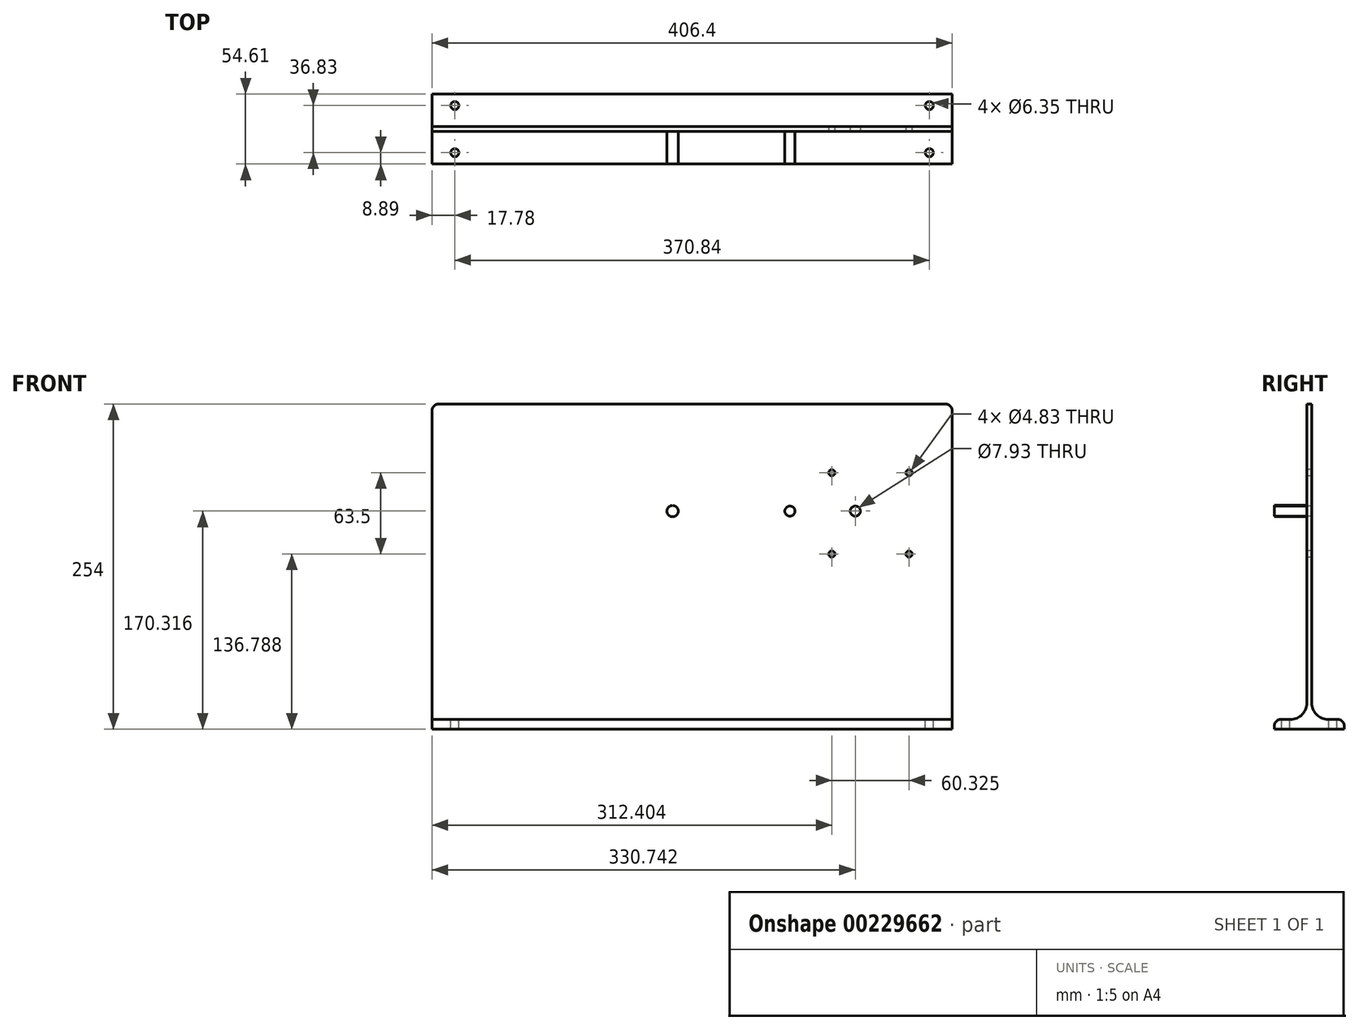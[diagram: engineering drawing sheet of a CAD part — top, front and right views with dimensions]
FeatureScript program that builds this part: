
annotation { "Feature Type Name" : "Feature", "Feature Type Description" : "" }
export const myFeature = defineFeature(function(context is Context, id is Id, definition is map)
    precondition{}
    {
        {
            var Q0;
            Q0=qCreatedBy(makeId("Front.planeOp"),FACE);
            var sketch = newSketch(context, id + "F0", { "sketchPlane" : qUnion([Q0])});
            skLineSegment(sketch, "E0.bottom", {"start": v(0, 0) * mm, "end": v(406.4, 0) * mm});
            skLineSegment(sketch, "E0.top", {"start": v(0, 254) * mm, "end": v(406.4, 254) * mm});
            skLineSegment(sketch, "E0.left", {"start": v(0, 0) * mm, "end": v(0, 254) * mm});
            skLineSegment(sketch, "E0.right", {"start": v(406.4, 0) * mm, "end": v(406.4, 254) * mm});
            skSolve(sketch);
        }
        {
            var Q0;
            Q0 = qSketchRegion(id + "F0", true);
            extrude(context, id + "F1", {"entities" : qUnion([Q0]), "depth" : 3.8 * mm});
        }
        {
            var Q0;
            Q0=makeQuery(id+"F1.opExtrude","SWEPT_FACE",FACE,{"disambiguationData":[OSD([sQuery(id+"F0.wireOp",EDGE,"E0.bottom")])]});
            var sketch = newSketch(context, id + "F2", { "sketchPlane" : qUnion([Q0])});
            skLineSegment(sketch, "E1.bottom", {"start": v(0, -25.4) * mm, "end": v(406.4, -25.4) * mm});
            skLineSegment(sketch, "E1.top", {"start": v(0, 29.21) * mm, "end": v(406.4, 29.21) * mm});
            skLineSegment(sketch, "E1.left", {"start": v(0, -25.4) * mm, "end": v(0, 29.21) * mm});
            skLineSegment(sketch, "E1.right", {"start": v(406.4, -25.4) * mm, "end": v(406.4, 29.21) * mm});
            skSolve(sketch);
        }
        {
            var Q0;
            Q0 = qSketchRegion(id + "F2", true);
            extrude(context, id + "F3", {"entities" : qUnion([Q0]), "operationType" : NewBodyOperationType.ADD, "oppositeDirection" : true, "depth" : 7.62 * mm});
        }
        {
            var Q0;
            Q0=makeQuery(id+"F3.boolean.opBoolean","INTERSECT",EDGE,{"derivedFrom":[makeQuery(id+"F1.opExtrude","CAP_FACE",FACE,{"disambiguationData":[OSD([sQuery(id+"F0.wireOp",EDGE,"E0.bottom"),sQuery(id+"F0.wireOp",EDGE,"E0.top"),sQuery(id+"F0.wireOp",EDGE,"E0.left"),sQuery(id+"F0.wireOp",EDGE,"E0.right")])],"isStart":true}),makeQuery(id+"F3.opExtrude","CAP_FACE",FACE,{"disambiguationData":[OSD([sQuery(id+"F2.wireOp",EDGE,"E1.bottom"),sQuery(id+"F2.wireOp",EDGE,"E1.top"),sQuery(id+"F2.wireOp",EDGE,"E1.left"),sQuery(id+"F2.wireOp",EDGE,"E1.right")])],"isStart":false})]});
            var Q1;
            Q1=makeQuery(id+"F3.boolean.opBoolean","INTERSECT",EDGE,{"derivedFrom":[makeQuery(id+"F1.opExtrude","CAP_FACE",FACE,{"disambiguationData":[OSD([sQuery(id+"F0.wireOp",EDGE,"E0.bottom"),sQuery(id+"F0.wireOp",EDGE,"E0.top"),sQuery(id+"F0.wireOp",EDGE,"E0.left"),sQuery(id+"F0.wireOp",EDGE,"E0.right")])],"isStart":false}),makeQuery(id+"F3.opExtrude","CAP_FACE",FACE,{"disambiguationData":[OSD([sQuery(id+"F2.wireOp",EDGE,"E1.bottom"),sQuery(id+"F2.wireOp",EDGE,"E1.top"),sQuery(id+"F2.wireOp",EDGE,"E1.left"),sQuery(id+"F2.wireOp",EDGE,"E1.right")])],"isStart":false})]});
            fillet(context, id + "F4", {"entities" : qUnion([Q0, Q1]), "radius" : 12.7 * mm, "tangentPropagation" : true, "allowEdgeOverflow" : false});
        }
        {
            var Q0;
            Q0=makeQuery(id+"F3.opExtrude","CAP_EDGE",EDGE,{"disambiguationData":[OSD([sQuery(id+"F2.wireOp",EDGE,"E1.top")])],"isStart":false});
            var Q1;
            Q1=makeQuery(id+"F3.opExtrude","CAP_EDGE",EDGE,{"disambiguationData":[OSD([sQuery(id+"F2.wireOp",EDGE,"E1.bottom")])],"isStart":false});
            var Q2;
            Q2=makeQuery(id+"F1.opExtrude","SWEPT_EDGE",EDGE,{"disambiguationData":[OSD([sQuery(id+"F0.wireOp",EDGE,"E0.top"),sQuery(id+"F0.wireOp",EDGE,"E0.right")])]});
            var Q3;
            Q3=makeQuery(id+"F1.opExtrude","SWEPT_EDGE",EDGE,{"disambiguationData":[OSD([sQuery(id+"F0.wireOp",EDGE,"E0.top"),sQuery(id+"F0.wireOp",EDGE,"E0.left")])]});
            fillet(context, id + "F5", {"entities" : qUnion([Q0, Q1, Q2, Q3]), "radius" : 5.08 * mm, "tangentPropagation" : true, "allowEdgeOverflow" : false});
        }
        {
            var Q0;
            Q0=makeQuery(id+"F1.opExtrude","CAP_FACE",FACE,{"disambiguationData":[OSD([sQuery(id+"F0.wireOp",EDGE,"E0.bottom"),sQuery(id+"F0.wireOp",EDGE,"E0.top"),sQuery(id+"F0.wireOp",EDGE,"E0.left"),sQuery(id+"F0.wireOp",EDGE,"E0.right")])],"isStart":false});
            var sketch = newSketch(context, id + "F6", { "sketchPlane" : qUnion([Q0])});
            skCircle(sketch, "E2", {"center": v(312.4, 200.29) * mm, "radius": 2.41 * mm});
            skCircle(sketch, "E3", {"center": v(372.73, 200.29) * mm, "radius": 2.41 * mm});
            skCircle(sketch, "E4", {"center": v(312.4, 136.79) * mm, "radius": 2.41 * mm});
            skCircle(sketch, "E5", {"center": v(372.73, 136.79) * mm, "radius": 2.41 * mm});
            skCircle(sketch, "E6", {"center": v(330.74, 170.32) * mm, "radius": 3.97 * mm});
            skLineSegment(sketch, "E7", {"start": v(312.4, 223.39) * mm, "end": v(312.4, 129.56) * mm, "construction": true});
            skLineSegment(sketch, "E8", {"start": v(312.4, 200.29) * mm, "end": v(398.76, 200.29) * mm, "construction": true});
            skSolve(sketch);
        }
        {
            var Q0;
            Q0 = qSketchRegion(id + "F6", true);
            extrude(context, id + "F7", {"entities" : qUnion([Q0]), "operationType" : NewBodyOperationType.REMOVE, "endBound" : BoundingType.THROUGH_ALL, "oppositeDirection" : true, "depth" : 25.4 * mm});
        }
        {
            var Q0;
            Q0=makeQuery(id+"F1.opExtrude","CAP_FACE",FACE,{"disambiguationData":[OSD([sQuery(id+"F0.wireOp",EDGE,"E0.bottom"),sQuery(id+"F0.wireOp",EDGE,"E0.top"),sQuery(id+"F0.wireOp",EDGE,"E0.left"),sQuery(id+"F0.wireOp",EDGE,"E0.right")])],"isStart":false});
            var sketch = newSketch(context, id + "F8", { "sketchPlane" : qUnion([Q0])});
            skCircle(sketch, "E9", {"center": v(279.65, 170.32) * mm, "radius": 3.96 * mm});
            skSolve(sketch);
        }
        {
            var Q0;
            Q0 = qSketchRegion(id + "F8", true);
            extrude(context, id + "F9", {"entities" : qUnion([Q0]), "operationType" : NewBodyOperationType.ADD, "depth" : 25.4 * mm});
        }
        {
            var Q0;
            Q0=makeQuery(id+"F1.opExtrude","CAP_FACE",FACE,{"disambiguationData":[OSD([sQuery(id+"F0.wireOp",EDGE,"E0.bottom"),sQuery(id+"F0.wireOp",EDGE,"E0.top"),sQuery(id+"F0.wireOp",EDGE,"E0.left"),sQuery(id+"F0.wireOp",EDGE,"E0.right")])],"isStart":false});
            var sketch = newSketch(context, id + "F10", { "sketchPlane" : qUnion([Q0])});
            skCircle(sketch, "E10", {"center": v(187.96, 170.32) * mm, "radius": 4.45 * mm});
            skSolve(sketch);
        }
        {
            var Q0;
            Q0 = qSketchRegion(id + "F10", true);
            extrude(context, id + "F11", {"entities" : qUnion([Q0]), "operationType" : NewBodyOperationType.ADD, "depth" : 25.4 * mm});
        }
        {
            var Q0;
            {var subQ1=sQuery(id+"F2.wireOp",EDGE,"E1.bottom");var subQ3=sQuery(id+"F2.wireOp",EDGE,"E1.right");var subQ4=sQuery(id+"F2.wireOp",EDGE,"E1.left");Q0=makeQuery(id+"F3.boolean.opBoolean","SPLIT",FACE,{"disambiguationData":[TD([makeQuery(id+"F3.opExtrude","SWEPT_FACE",FACE,{"disambiguationData":[OSD([subQ1])]})])],"derivedFrom":makeQuery(id+"F3.opExtrude","CAP_FACE",FACE,{"disambiguationData":[OSD([subQ1,sQuery(id+"F2.wireOp",EDGE,"E1.top"),subQ4,subQ3])],"isStart":false})});}
            var sketch = newSketch(context, id + "F12", { "sketchPlane" : qUnion([Q0])});
            skPoint(sketch, "E11", {"position": v(17.78, 16.51) * mm});
            skPoint(sketch, "E11.positionSnap0", {"position": v(0, 16.51) * mm});
            skPoint(sketch, "E12", {"position": v(388.62, 16.51) * mm});
            skPoint(sketch, "E13", {"position": v(388.62, -20.32) * mm});
            skPoint(sketch, "E13.positionSnap0", {"position": v(406.4, -20.32) * mm});
            skPoint(sketch, "E14", {"position": v(17.78, -20.32) * mm});
            skSolve(sketch);
        }
        {
            var Q0;
            Q0=sQuery(id+"F12.wireOp",VERTEX,"E12");
            var Q1;
            Q1=sQuery(id+"F12.wireOp",VERTEX,"E13");
            var Q2;
            Q2=sQuery(id+"F12.wireOp",VERTEX,"E11");
            var Q3;
            Q3=sQuery(id+"F12.wireOp",VERTEX,"E14");
            var Q4;
            Q4=makeQuery(id+"F1.opExtrude","SWEPT_BODY",BODY,{"disambiguationData":[OSD([sQuery(id+"F0.wireOp",EDGE,"E0.bottom"),sQuery(id+"F0.wireOp",EDGE,"E0.top"),sQuery(id+"F0.wireOp",EDGE,"E0.left"),sQuery(id+"F0.wireOp",EDGE,"E0.right")])]});
            hole(context, id + "F13", {"style" : HoleStyle.SIMPLE, "endStyle" : HoleEndStyle.THROUGH, "holeDiameter" : 6.35 * mm, "locations" : qUnion([Q0, Q1, Q2, Q3]), "scope" : qUnion([Q4]), "isTappedThrough" : true});
        }
    });
